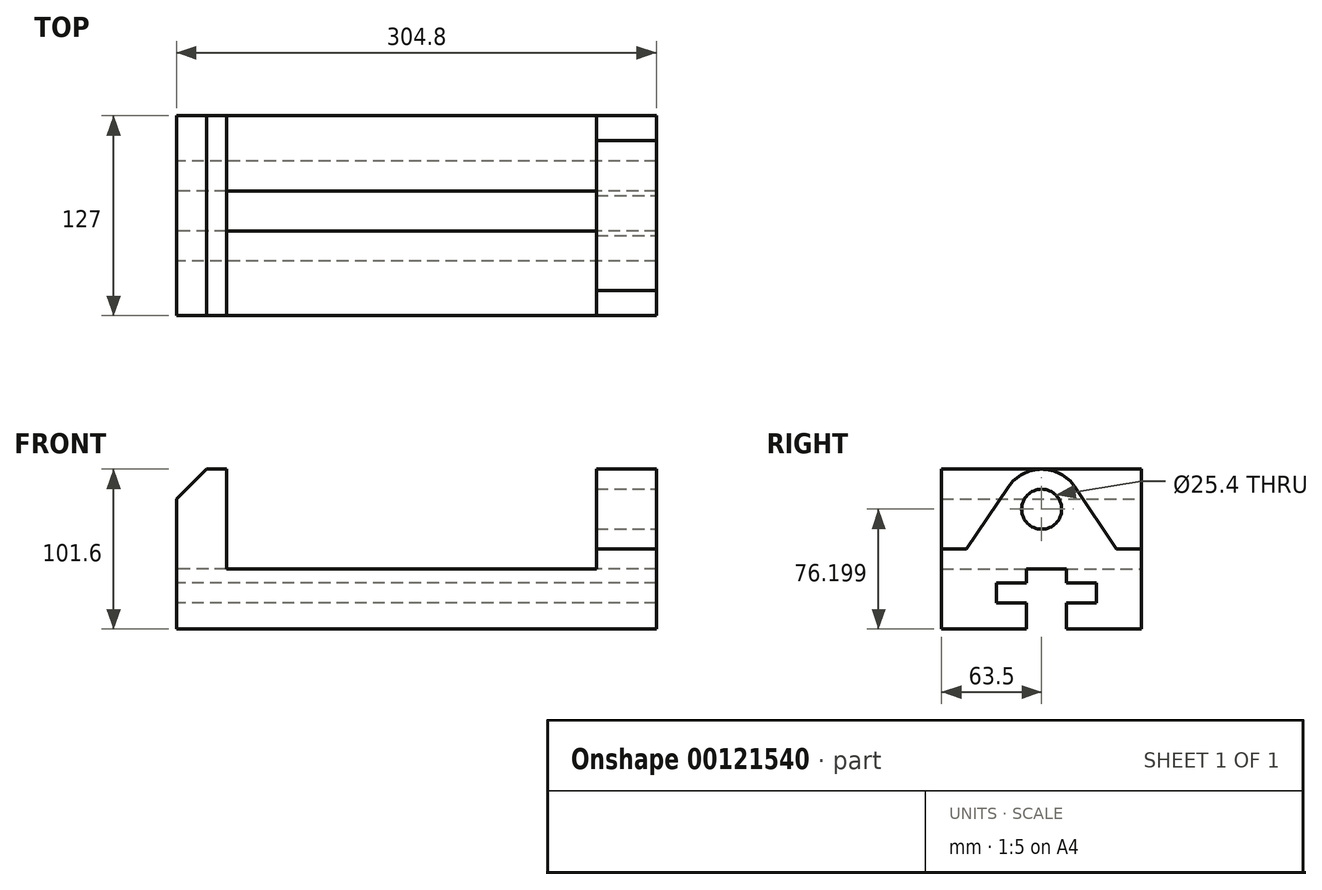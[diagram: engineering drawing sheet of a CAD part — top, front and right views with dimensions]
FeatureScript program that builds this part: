
annotation { "Feature Type Name" : "Feature", "Feature Type Description" : "" }
export const myFeature = defineFeature(function(context is Context, id is Id, definition is map)
    precondition{}
    {
        {
            var Q0;
            Q0=qCreatedBy(makeId("Front.planeOp"),FACE);
            var sketch = newSketch(context, id + "F0", { "sketchPlane" : qUnion([Q0])});
            skLineSegment(sketch, "E0", {"start": v(0, 101.6) * mm, "end": v(0, 0) * mm});
            skLineSegment(sketch, "E1", {"start": v(0, 0) * mm, "end": v(304.8, 0) * mm});
            skLineSegment(sketch, "E2", {"start": v(304.8, 0) * mm, "end": v(304.8, 101.6) * mm});
            skLineSegment(sketch, "E3", {"start": v(304.8, 101.6) * mm, "end": v(266.7, 101.6) * mm});
            skLineSegment(sketch, "E4", {"start": v(266.7, 101.6) * mm, "end": v(266.7, 38.1) * mm});
            skLineSegment(sketch, "E5", {"start": v(266.7, 38.1) * mm, "end": v(31.75, 38.1) * mm});
            skLineSegment(sketch, "E6", {"start": v(31.75, 38.1) * mm, "end": v(31.75, 101.6) * mm});
            skLineSegment(sketch, "E7", {"start": v(31.75, 101.6) * mm, "end": v(0, 101.6) * mm});
            skSolve(sketch);
        }
        {
            var Q0;
            Q0 = qSketchRegion(id + "F0", true);
            extrude(context, id + "F1", {"entities" : qUnion([Q0]), "depth" : 127 * mm});
        }
        {
            var Q0;
            Q0=makeQuery(id+"F1.opExtrude","SWEPT_EDGE",EDGE,{"disambiguationData":[OSD([sQuery(id+"F0.wireOp",EDGE,"E0"),sQuery(id+"F0.wireOp",EDGE,"E7")])]});
            chamfer(context, id + "F2", {"entities" : qUnion([Q0]), "width" : 19.05 * mm, "tangentPropagation" : true});
        }
        {
            var Q0;
            Q0=qCreatedBy(makeId("Right.planeOp"),FACE);
            var sketch = newSketch(context, id + "F3", { "sketchPlane" : qUnion([Q0])});
            skLineSegment(sketch, "E8", {"start": v(0, 50.8) * mm, "end": v(0, 0) * mm});
            skLineSegment(sketch, "E9", {"start": v(-47.85, 0) * mm, "end": v(-47.85, 16.51) * mm});
            skLineSegment(sketch, "E10", {"start": v(-47.85, 16.51) * mm, "end": v(-28.8, 16.51) * mm});
            skLineSegment(sketch, "E11", {"start": v(-28.8, 16.51) * mm, "end": v(-28.8, 29.21) * mm});
            skLineSegment(sketch, "E12", {"start": v(-28.8, 29.21) * mm, "end": v(-47.85, 29.21) * mm});
            skLineSegment(sketch, "E13", {"start": v(-47.85, 29.21) * mm, "end": v(-47.85, 38.1) * mm});
            skLineSegment(sketch, "E14", {"start": v(-47.85, 38.1) * mm, "end": v(-73.25, 38.1) * mm});
            skLineSegment(sketch, "E15", {"start": v(-73.25, 38.1) * mm, "end": v(-73.25, 29.21) * mm});
            skLineSegment(sketch, "E16", {"start": v(-73.25, 29.21) * mm, "end": v(-92.3, 29.21) * mm});
            skLineSegment(sketch, "E17", {"start": v(-92.3, 29.21) * mm, "end": v(-92.3, 16.51) * mm});
            skLineSegment(sketch, "E18", {"start": v(-92.3, 16.51) * mm, "end": v(-73.25, 16.51) * mm});
            skLineSegment(sketch, "E19", {"start": v(-73.25, 16.51) * mm, "end": v(-73.25, 0) * mm});
            skLineSegment(sketch, "E20", {"start": v(-127, 0) * mm, "end": v(-127, 50.8) * mm});
            skLineSegment(sketch, "E21", {"start": v(-127, 50.8) * mm, "end": v(-111.13, 50.8) * mm});
            skLineSegment(sketch, "E22", {"start": v(0, 50.8) * mm, "end": v(-15.87, 50.8) * mm});
            skLineSegment(sketch, "E23", {"start": v(0, 0) * mm, "end": v(-127, 0) * mm});
            skSolve(sketch);
        }
        {
            var Q0;
            Q0 = qSketchRegion(id + "F3", true);
            var Q1;
            Q1=makeQuery(id+"F1.opExtrude","SWEPT_FACE",FACE,{"disambiguationData":[OSD([sQuery(id+"F0.wireOp",EDGE,"E2")])]});
            extrude(context, id + "F4", {"entities" : qUnion([Q0]), "operationType" : NewBodyOperationType.REMOVE, "endBound" : BoundingType.UP_TO_SURFACE, "endBoundEntityFace" : qUnion([Q1]), "depth" : 25.4 * mm});
        }
        {
            var Q0;
            Q0=makeQuery(id+"F1.opExtrude","SWEPT_FACE",FACE,{"disambiguationData":[OSD([sQuery(id+"F0.wireOp",EDGE,"E2")])]});
            var sketch = newSketch(context, id + "F5", { "sketchPlane" : qUnion([Q0])});
            skLineSegment(sketch, "E24", {"start": v(-127, 50.8) * mm, "end": v(-111.12, 50.8) * mm});
            skLineSegment(sketch, "E25", {"start": v(-111.13, 50.8) * mm, "end": v(-84.6, 90.35) * mm});
            skArc(sketch, "E26", {"start": v(-84.6, 90.35) * mm, "mid": v(-63.5, 101.6) * mm, "end": v(-42.4, 90.35) * mm});
            skLineSegment(sketch, "E27", {"start": v(-42.4, 90.35) * mm, "end": v(-15.88, 50.8) * mm});
            skLineSegment(sketch, "E28", {"start": v(-15.88, 50.8) * mm, "end": v(0, 50.8) * mm});
            skLineSegment(sketch, "E29", {"start": v(-127, 50.8) * mm, "end": v(-127, 101.6) * mm});
            skLineSegment(sketch, "E30", {"start": v(-127, 101.6) * mm, "end": v(0, 101.6) * mm});
            skLineSegment(sketch, "E31", {"start": v(0, 101.6) * mm, "end": v(0, 50.8) * mm});
            skCircle(sketch, "E32", {"center": v(-63.5, 76.2) * mm, "radius": 12.7 * mm});
            skSolve(sketch);
        }
        {
            var Q0;
            Q0 = qSketchRegion(id + "F5", true);
            extrude(context, id + "F6", {"entities" : qUnion([Q0]), "operationType" : NewBodyOperationType.REMOVE, "endBound" : BoundingType.UP_TO_NEXT, "oppositeDirection" : true, "depth" : 25.4 * mm});
        }
    });
